SOLIDWORKS PART (.sldprt)
format: sldprt  version: not decoded by parser v0  size: 400,896 bytes
history: native  units: mm
features: sketch x3, cut_extrude x2, pattern_linear x2, material x1, extrude x1 + 1 further entry (+14 scaffold rows collapsed; 3 parser-record rows omitted)
feature tree (27):
  scaffold x14  (default folders/planes/origin — collapsed)
  material  "Material <not specified>"
  parser-record x3  (decoder bookkeeping rows leaked as tree rows — omitted from the tree; the rows remain in map.json)
  "Design Table"
  sketch  "Sketch1"  dims[c1.D4=3.175mm c1.D5=3.1496mm c1.InnerRadius=6.35mm c1.LengthZ=38.1mm c1.HeightY=38.1mm c1.D3=3.175mm c2.D4=~7.352994mm c2.Thick=6.35mm c2.D8=63.5mm]
  extrude  "Base Extrude"  Depth=33.274mm WidthX=33.274mm
  sketch  "Sketch2"  dims[HoleDiam=8.3312mm D3=~9.16583mm HoleZ=19.05mm HoleX=16.637mm]
  cut_extrude  "Hole"  Depth=159.385mm
  pattern_linear  "Hole Pattern"  Count1=2 Count2=2 Spacing1=38.1mm Spacing2=38.1mm NumberX=2 SpacingX=38.1mm NumberZ=2 SpacingZ=38.1mm
  sketch  "Sketch3"  dims[c1.D2=~13.14096mm c1.D3=6.5278mm c2.D2=6.5278mm c2.SlotWidth=8.3312mm c2.SlotY=12.7mm c2.SlotX=16.637mm c2.SlotLength=21.0312mm]
  cut_extrude  "Slot"  Depth=57.785mm
  pattern_linear  "Slot Pattern"  Count1=2 Count2=1 Spacing1=38.1mm Spacing2=38.1mm NumberX=2 SpacingX=38.1mm NumberY=1 SpacingY=38.1mm
decode coverage: 8 of 8 modeling features carry decoded parameters; 1 rows unclassified (native names shown)
note: ~ marks probable driven/reference dimensions
note: suppression state not decoded; provenance and decode notes live in map.json
